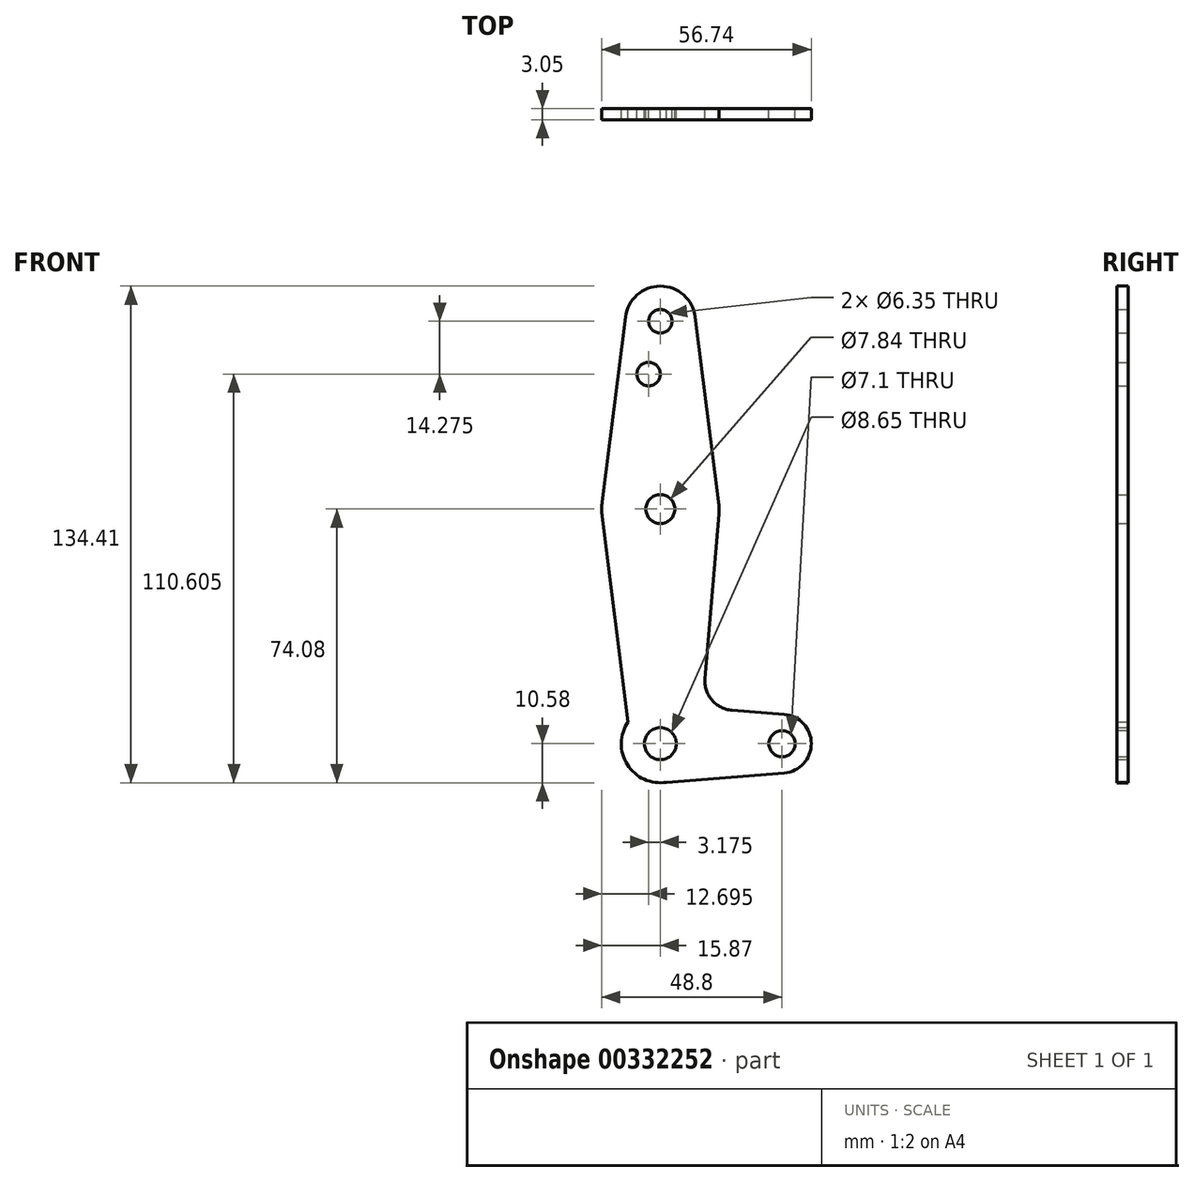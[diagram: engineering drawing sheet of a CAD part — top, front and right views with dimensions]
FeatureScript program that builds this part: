
annotation { "Feature Type Name" : "Feature", "Feature Type Description" : "" }
export const myFeature = defineFeature(function(context is Context, id is Id, definition is map)
    precondition{}
    {
        {
            var Q0;
            Q0=qCreatedBy(makeId("Front.planeOp"),FACE);
            var sketch = newSketch(context, id + "F0", { "sketchPlane" : qUnion([Q0])});
            skLineSegment(sketch, "E0", {"start": v(0, 0) * mm, "end": v(0, 4.32) * mm});
            skLineSegment(sketch, "E1", {"start": v(0, 63.5) * mm, "end": v(0, 114.3) * mm});
            skLineSegment(sketch, "E2", {"start": v(0, 0) * mm, "end": v(4.32, 0) * mm});
            skCircle(sketch, "E3", {"center": v(0, 114.3) * mm, "radius": 9.53 * mm});
            skCircle(sketch, "E4", {"center": v(0, 63.5) * mm, "radius": 15.88 * mm});
            skCircle(sketch, "E5", {"center": v(0, 0) * mm, "radius": 10.58 * mm});
            skCircle(sketch, "E6", {"center": v(32.93, 0) * mm, "radius": 7.94 * mm});
            skLineSegment(sketch, "E7", {"start": v(9.45, 115.5) * mm, "end": v(15.75, 65.48) * mm});
            skLineSegment(sketch, "E8", {"start": v(-9.45, 115.5) * mm, "end": v(-15.75, 65.48) * mm});
            skLineSegment(sketch, "E9", {"start": v(-15.75, 65.48) * mm, "end": v(-15.75, 61.52) * mm});
            skLineSegment(sketch, "E10", {"start": v(-15.75, 61.52) * mm, "end": v(-8.75, 5.94) * mm});
            skLineSegment(sketch, "E11", {"start": v(15.82, 62.18) * mm, "end": v(12.09, 17.63) * mm});
            skLineSegment(sketch, "E12", {"start": v(19.38, 9.04) * mm, "end": v(33.56, 7.91) * mm});
            skLineSegment(sketch, "E13", {"start": v(0, -10.58) * mm, "end": v(33.56, -7.91) * mm});
            skCircle(sketch, "E14", {"center": v(0, 114.3) * mm, "radius": 3.18 * mm});
            skCircle(sketch, "E15", {"center": v(0, 63.5) * mm, "radius": 3.92 * mm});
            skCircle(sketch, "E16", {"center": v(0, 0) * mm, "radius": 4.32 * mm});
            skCircle(sketch, "E17", {"center": v(32.93, 0) * mm, "radius": 3.55 * mm});
            skCircle(sketch, "E18", {"center": v(-3.18, 100.03) * mm, "radius": 3.18 * mm});
            skArc(sketch, "E19.filletArc", {"start": v(12.09, 17.63) * mm, "mid": v(13.95, 11.82) * mm, "end": v(19.38, 9.04) * mm});
            skLineSegment(sketch, "E20.trimOffspring", {"start": v(0, 10.58) * mm, "end": v(0, 63.5) * mm});
            skLineSegment(sketch, "E21.trimOffspring", {"start": v(10.58, 0) * mm, "end": v(32.93, 0) * mm});
            skSolve(sketch);
        }
        {
            var Q0;
            Q0 = qSketchRegion(id + "F0", true);
            extrude(context, id + "F1", {"entities" : qUnion([Q0]), "depth" : 3.05 * mm});
        }
    });
